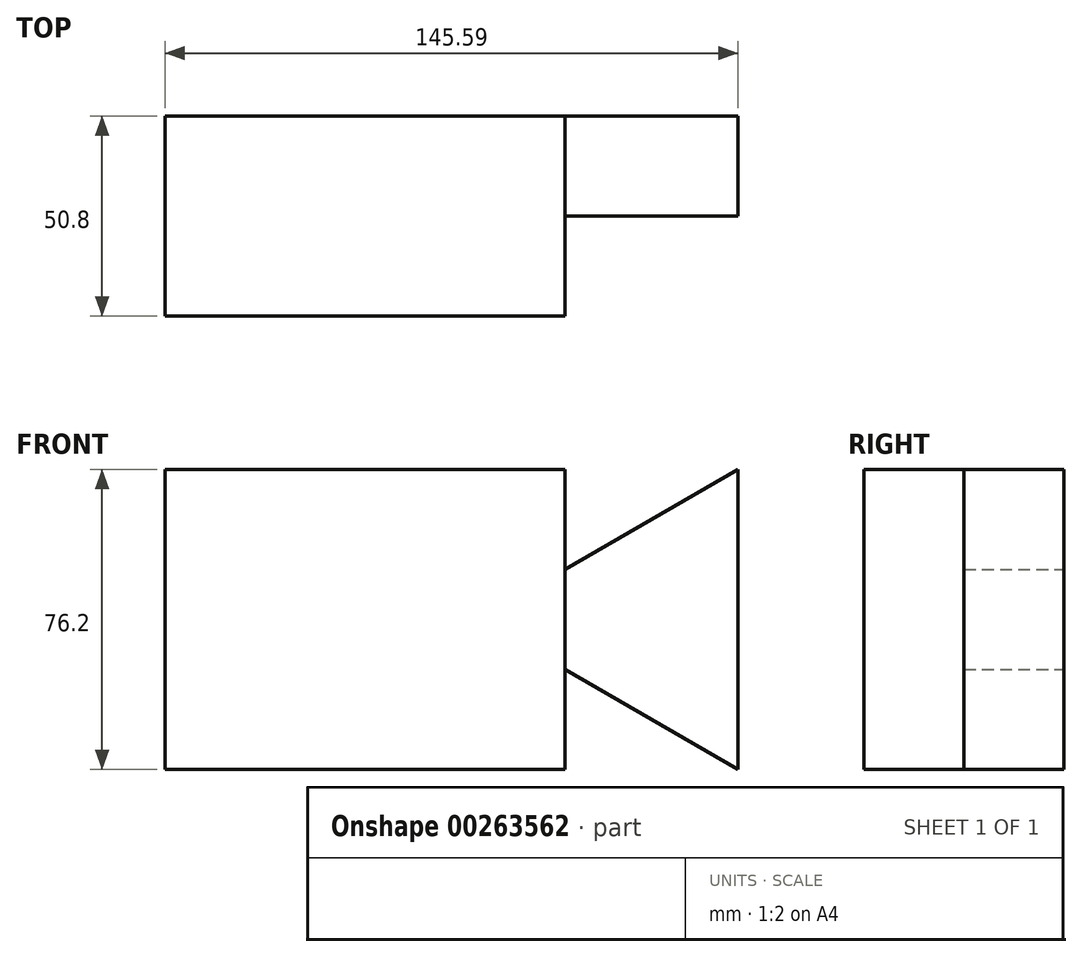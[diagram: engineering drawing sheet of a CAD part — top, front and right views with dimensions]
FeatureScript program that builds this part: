
annotation { "Feature Type Name" : "Feature", "Feature Type Description" : "" }
export const myFeature = defineFeature(function(context is Context, id is Id, definition is map)
    precondition{}
    {
        {
            var Q0;
            Q0=qCreatedBy(makeId("Front.planeOp"),FACE);
            var sketch = newSketch(context, id + "F0", { "sketchPlane" : qUnion([Q0])});
            skLineSegment(sketch, "E0", {"start": v(0, 0) * mm, "end": v(0, -76.2) * mm});
            skLineSegment(sketch, "E1", {"start": v(0, 0) * mm, "end": v(-101.6, 0) * mm});
            skLineSegment(sketch, "E2", {"start": v(-101.6, 0) * mm, "end": v(-101.6, -76.2) * mm});
            skLineSegment(sketch, "E3", {"start": v(-101.6, -76.2) * mm, "end": v(0, -76.2) * mm});
            skLineSegment(sketch, "E4", {"start": v(0, 0) * mm, "end": v(0, -25.4) * mm});
            skLineSegment(sketch, "E5", {"start": v(0, -76.2) * mm, "end": v(0, -50.8) * mm});
            skLineSegment(sketch, "E6", {"start": v(0, -50.8) * mm, "end": v(44, -76.2) * mm});
            skLineSegment(sketch, "E7", {"start": v(0, -25.4) * mm, "end": v(44, 0) * mm});
            skLineSegment(sketch, "E8", {"start": v(44, 0) * mm, "end": v(44, -76.2) * mm});
            skSolve(sketch);
        }
        {
            var Q0;
            Q0=makeQuery(id+"F0.imprint","IMPRINT",FACE,{"disambiguationData":[TD([[makeQuery(id+"F0.imprint","IMPRINT",EDGE,{"derivedFrom":sQuery(id+"F0.wireOp",EDGE,"E0")}),-1.0]])]});
            extrude(context, id + "F1", {"entities" : qUnion([Q0]), "depth" : 50.8 * mm});
        }
        {
            var Q0;
            Q0=makeQuery(id+"F0.imprint","IMPRINT",FACE,{"disambiguationData":[TD([[makeQuery(id+"F0.imprint","IMPRINT",EDGE,{"derivedFrom":sQuery(id+"F0.wireOp",EDGE,"E0")}),1.0]])]});
            extrude(context, id + "F2", {"entities" : qUnion([Q0]), "operationType" : NewBodyOperationType.ADD, "depth" : 25.4 * mm});
        }
    });
